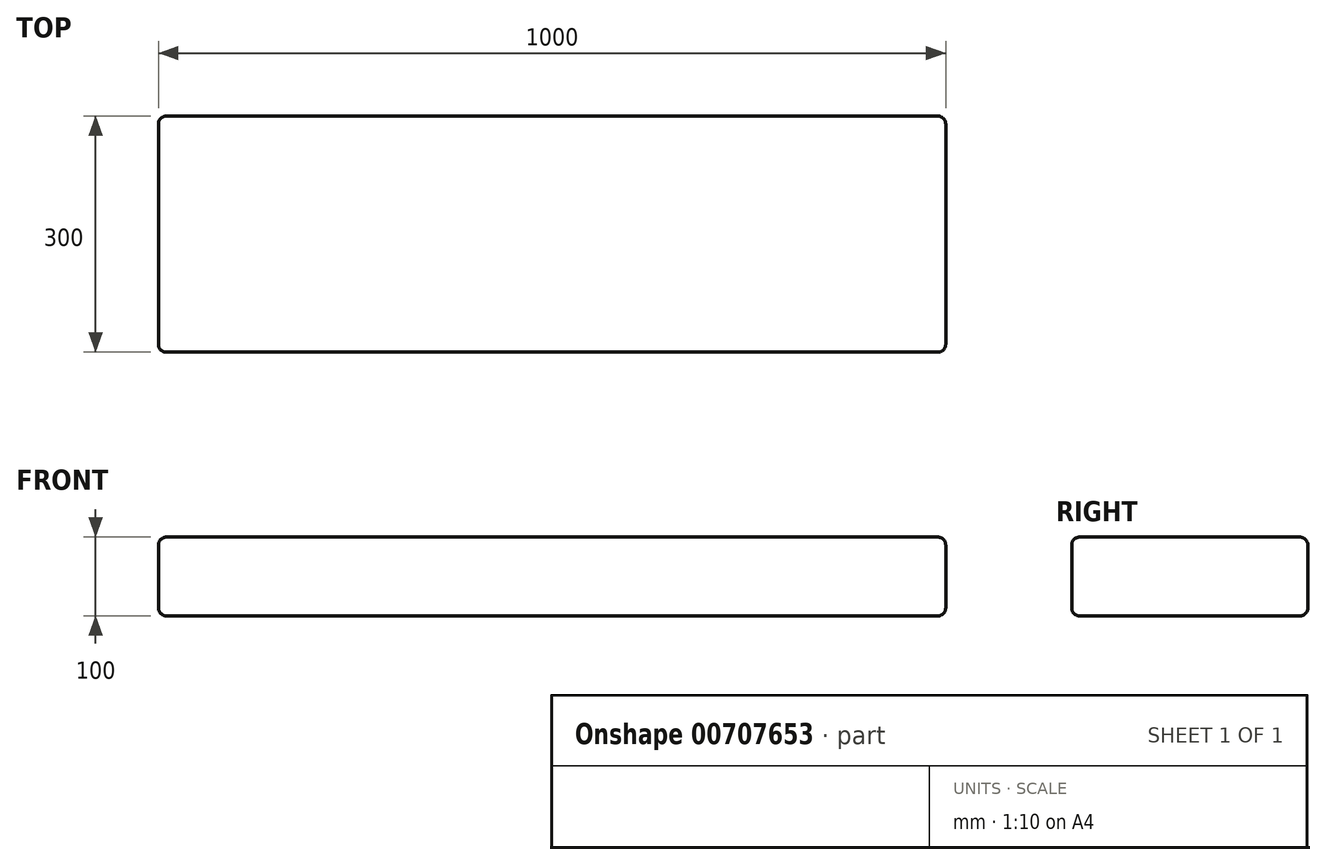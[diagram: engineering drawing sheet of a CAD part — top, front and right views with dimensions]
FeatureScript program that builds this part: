
annotation { "Feature Type Name" : "Feature", "Feature Type Description" : "" }
export const myFeature = defineFeature(function(context is Context, id is Id, definition is map)
    precondition{}
    {
        {
            var Q0;
            Q0=qCreatedBy(makeId("Top.planeOp"),FACE);
            var sketch = newSketch(context, id + "F0", { "sketchPlane" : qUnion([Q0])});
            skLineSegment(sketch, "E0.bottom", {"start": v(500, 150) * mm, "end": v(-500, 150) * mm});
            skLineSegment(sketch, "E0.top", {"start": v(500, -150) * mm, "end": v(-500, -150) * mm});
            skLineSegment(sketch, "E0.left", {"start": v(500, 150) * mm, "end": v(500, -150) * mm});
            skLineSegment(sketch, "E0.right", {"start": v(-500, 150) * mm, "end": v(-500, -150) * mm});
            skPoint(sketch, "E0.middle", {"position": v(0, 0) * mm});
            skSolve(sketch);
        }
        {
            var Q0;
            Q0=makeQuery(id+"F0.imprint","IMPRINT",FACE,{"disambiguationData":[TD([[makeQuery(id+"F0.imprint","IMPRINT",EDGE,{"derivedFrom":sQuery(id+"F0.wireOp",EDGE,"E0.bottom")}),1.0]])]});
            extrude(context, id + "F1", {"entities" : qUnion([Q0]), "depth" : 100 * mm, "offsetDistance" : 25 * mm});
        }
        {
            var Q0;
            Q0=makeQuery(id+"F1.opExtrude","CAP_EDGE",EDGE,{"disambiguationData":[OSD([sQuery(id+"F0.wireOp",EDGE,"E0.top")])],"isStart":false});
            var Q1;
            Q1=makeQuery(id+"F1.opExtrude","CAP_EDGE",EDGE,{"disambiguationData":[OSD([sQuery(id+"F0.wireOp",EDGE,"E0.right")])],"isStart":false});
            var Q2;
            Q2=makeQuery(id+"F1.opExtrude","CAP_EDGE",EDGE,{"disambiguationData":[OSD([sQuery(id+"F0.wireOp",EDGE,"E0.bottom")])],"isStart":false});
            var Q3;
            Q3=makeQuery(id+"F1.opExtrude","CAP_EDGE",EDGE,{"disambiguationData":[OSD([sQuery(id+"F0.wireOp",EDGE,"E0.left")])],"isStart":false});
            var Q4;
            Q4=makeQuery(id+"F1.opExtrude","SWEPT_EDGE",EDGE,{"disambiguationData":[OSD([sQuery(id+"F0.wireOp",EDGE,"E0.bottom"),sQuery(id+"F0.wireOp",EDGE,"E0.left")])]});
            var Q5;
            Q5=makeQuery(id+"F1.opExtrude","SWEPT_EDGE",EDGE,{"disambiguationData":[OSD([sQuery(id+"F0.wireOp",EDGE,"E0.top"),sQuery(id+"F0.wireOp",EDGE,"E0.left")])]});
            var Q6;
            Q6=makeQuery(id+"F1.opExtrude","SWEPT_FACE",FACE,{"disambiguationData":[OSD([sQuery(id+"F0.wireOp",EDGE,"E0.top")])]});
            var Q7;
            Q7=makeQuery(id+"F1.opExtrude","SWEPT_FACE",FACE,{"disambiguationData":[OSD([sQuery(id+"F0.wireOp",EDGE,"E0.left")])]});
            var Q8;
            Q8=makeQuery(id+"F1.opExtrude","CAP_FACE",FACE,{"disambiguationData":[OSD([sQuery(id+"F0.wireOp",EDGE,"E0.bottom"),sQuery(id+"F0.wireOp",EDGE,"E0.top"),sQuery(id+"F0.wireOp",EDGE,"E0.left"),sQuery(id+"F0.wireOp",EDGE,"E0.right")])],"isStart":true});
            var Q9;
            Q9=makeQuery(id+"F1.opExtrude","SWEPT_FACE",FACE,{"disambiguationData":[OSD([sQuery(id+"F0.wireOp",EDGE,"E0.right")])]});
            fillet(context, id + "F2", {"entities" : qUnion([Q0, Q1, Q2, Q3, Q4, Q5, Q6, Q7, Q8, Q9]), "radius" : 10 * mm, "tangentPropagation" : true, "allowEdgeOverflow" : false});
        }
    });
